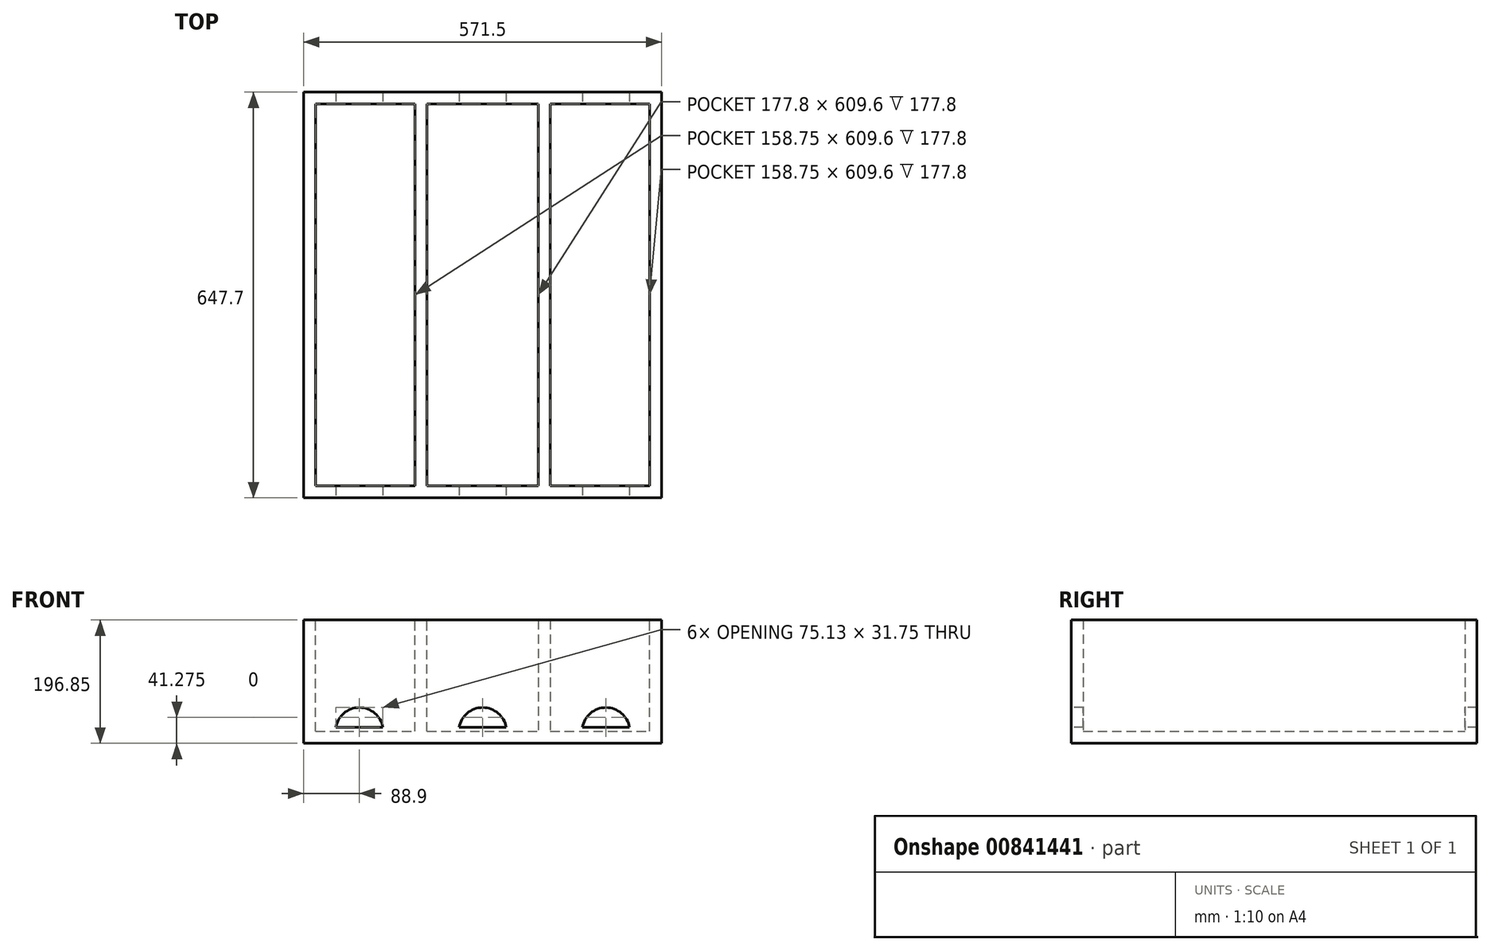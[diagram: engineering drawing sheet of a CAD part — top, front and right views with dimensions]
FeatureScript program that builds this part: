
annotation { "Feature Type Name" : "Feature", "Feature Type Description" : "" }
export const myFeature = defineFeature(function(context is Context, id is Id, definition is map)
    precondition{}
    {
        {
            var Q0;
            Q0=qCreatedBy(makeId("Front.planeOp"),FACE);
            var sketch = newSketch(context, id + "F0", { "sketchPlane" : qUnion([Q0])});
            skLineSegment(sketch, "E0", {"start": v(0, 86) * mm, "end": v(0, -86.18) * mm, "construction": true});
            skLineSegment(sketch, "E1", {"start": v(-97.69, 0) * mm, "end": v(113.87, 0) * mm, "construction": true});
            skLineSegment(sketch, "E2.bottom", {"start": v(-285.75, 0) * mm, "end": v(285.75, 0) * mm});
            skLineSegment(sketch, "E2.top", {"start": v(-285.75, 196.85) * mm, "end": v(285.75, 196.85) * mm});
            skLineSegment(sketch, "E2.left", {"start": v(-285.75, 0) * mm, "end": v(-285.75, 196.85) * mm});
            skLineSegment(sketch, "E2.right", {"start": v(285.75, 0) * mm, "end": v(285.75, 196.85) * mm});
            skSolve(sketch);
        }
        {
            var Q0;
            Q0 = qSketchRegion(id + "F0", true);
            extrude(context, id + "F1", {"entities" : qUnion([Q0]), "endBound" : BoundingType.SYMMETRIC, "depth" : 647.7 * mm, "offsetDistance" : 25.4 * mm});
        }
        {
            var Q0;
            Q0=makeQuery(id+"F1.opExtrude","SWEPT_FACE",FACE,{"disambiguationData":[OSD([sQuery(id+"F0.wireOp",EDGE,"E2.top")])]});
            shell(context, id + "F2", {"entities" : qUnion([Q0]), "thickness" : 19.05 * mm});
        }
        {
            var Q0;
            Q0=makeQuery(id+"F1.opExtrude","CAP_FACE",FACE,{"disambiguationData":[OSD([sQuery(id+"F0.wireOp",EDGE,"E2.bottom"),sQuery(id+"F0.wireOp",EDGE,"E2.top"),sQuery(id+"F0.wireOp",EDGE,"E2.left"),sQuery(id+"F0.wireOp",EDGE,"E2.right")])],"isStart":false});
            var sketch = newSketch(context, id + "F3", { "sketchPlane" : qUnion([Q0])});
            skArc(sketch, "E3", {"start": v(-159.28, 25.4) * mm, "mid": v(-196.85, 57.15) * mm, "end": v(-234.42, 25.4) * mm});
            skArc(sketch, "E4", {"start": v(37.57, 25.4) * mm, "mid": v(0, 57.15) * mm, "end": v(-37.57, 25.4) * mm});
            skLineSegment(sketch, "E5", {"start": v(0, -16.77) * mm, "end": v(0, 147.5) * mm, "construction": true});
            skArc(sketch, "E6.MirrorC", {"start": v(159.28, 25.4) * mm, "mid": v(196.85, 57.15) * mm, "end": v(234.42, 25.4) * mm});
            skLineSegment(sketch, "E7", {"start": v(-234.42, 25.4) * mm, "end": v(-159.28, 25.4) * mm});
            skLineSegment(sketch, "E8.trimOffspring", {"start": v(159.28, 25.4) * mm, "end": v(234.42, 25.4) * mm});
            skLineSegment(sketch, "E9.trimOffspring", {"start": v(-37.57, 25.4) * mm, "end": v(37.57, 25.4) * mm});
            skSolve(sketch);
        }
        {
            var Q0;
            Q0 = qSketchRegion(id + "F3", true);
            extrude(context, id + "F4", {"entities" : qUnion([Q0]), "operationType" : NewBodyOperationType.REMOVE, "endBound" : BoundingType.THROUGH_ALL, "oppositeDirection" : true, "depth" : 25.4 * mm, "offsetDistance" : 25.4 * mm});
        }
        {
            var Q0;
            Q0=qCreatedBy(makeId("Front.planeOp"),FACE);
            var sketch = newSketch(context, id + "F5", { "sketchPlane" : qUnion([Q0])});
            skLineSegment(sketch, "E10.bottom", {"start": v(-107.95, 19.05) * mm, "end": v(-88.9, 19.05) * mm});
            skLineSegment(sketch, "E10.top", {"start": v(-107.95, 196.85) * mm, "end": v(-88.9, 196.85) * mm});
            skLineSegment(sketch, "E10.left", {"start": v(-107.95, 19.05) * mm, "end": v(-107.95, 196.85) * mm});
            skLineSegment(sketch, "E10.right", {"start": v(-88.9, 19.05) * mm, "end": v(-88.9, 196.85) * mm});
            skLineSegment(sketch, "E11.bottom", {"start": v(88.9, 196.85) * mm, "end": v(107.95, 196.85) * mm});
            skLineSegment(sketch, "E11.top", {"start": v(88.9, 19.05) * mm, "end": v(107.95, 19.05) * mm});
            skLineSegment(sketch, "E11.left", {"start": v(88.9, 196.85) * mm, "end": v(88.9, 19.05) * mm});
            skLineSegment(sketch, "E11.right", {"start": v(107.95, 196.85) * mm, "end": v(107.95, 19.05) * mm});
            skLineSegment(sketch, "E12", {"start": v(0, -21.15) * mm, "end": v(0, 165.34) * mm, "construction": true});
            skSolve(sketch);
        }
        {
            var Q0;
            Q0 = qSketchRegion(id + "F5", true);
            var Q1;
            {var subQ0=sQuery(id+"F0.wireOp",EDGE,"E2.right");var subQ1=sQuery(id+"F0.wireOp",EDGE,"E2.left");var subQ2=sQuery(id+"F0.wireOp",EDGE,"E2.top");var subQ3=sQuery(id+"F0.wireOp",EDGE,"E2.bottom");Q1=makeQuery(id+"F2.opShell","OFFSET_FACE",FACE,{"disambiguationData":[OSD([subQ3,subQ2,subQ1,subQ0]),TDD([makeQuery(id+"F1.opExtrude","CAP_FACE",FACE,{"disambiguationData":[OSD([subQ3,subQ2,subQ1,subQ0])],"isStart":false})])]});}
            var Q2;
            {var subQ0=sQuery(id+"F0.wireOp",EDGE,"E2.right");var subQ1=sQuery(id+"F0.wireOp",EDGE,"E2.left");var subQ2=sQuery(id+"F0.wireOp",EDGE,"E2.top");var subQ3=sQuery(id+"F0.wireOp",EDGE,"E2.bottom");Q2=makeQuery(id+"F2.opShell","OFFSET_FACE",FACE,{"disambiguationData":[OSD([subQ3,subQ2,subQ1,subQ0]),TDD([makeQuery(id+"F1.opExtrude","CAP_FACE",FACE,{"disambiguationData":[OSD([subQ3,subQ2,subQ1,subQ0])],"isStart":true})])]});}
            extrude(context, id + "F6", {"entities" : qUnion([Q0]), "operationType" : NewBodyOperationType.ADD, "endBound" : BoundingType.UP_TO_SURFACE, "depth" : 25.4 * mm, "endBoundEntityFace" : qUnion([Q1]), "offsetDistance" : 25.4 * mm, "hasSecondDirection" : true, "secondDirectionBound" : SecondDirectionBoundingType.UP_TO_SURFACE, "secondDirectionOppositeDirection" : true, "secondDirectionDepth" : 25.4 * mm, "secondDirectionBoundEntityFace" : qUnion([Q2])});
        }
    });
